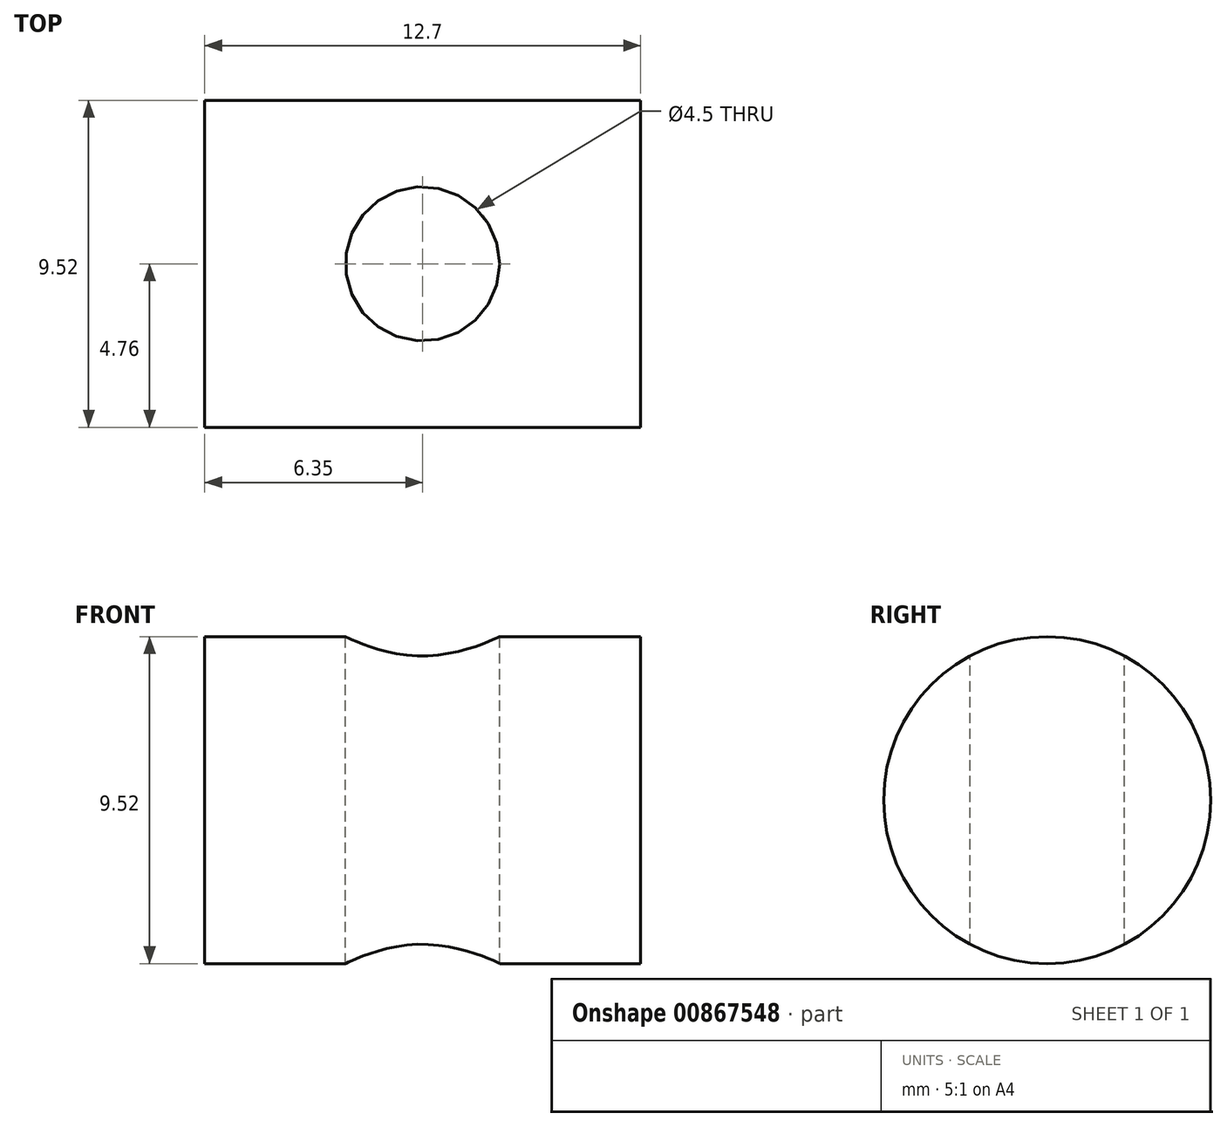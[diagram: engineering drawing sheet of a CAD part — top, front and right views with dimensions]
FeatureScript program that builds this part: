
annotation { "Feature Type Name" : "Feature", "Feature Type Description" : "" }
export const myFeature = defineFeature(function(context is Context, id is Id, definition is map)
    precondition{}
    {
        {
            var Q0;
            Q0=qCreatedBy(makeId("Right.planeOp"),FACE);
            var sketch = newSketch(context, id + "F0", { "sketchPlane" : qUnion([Q0])});
            skCircle(sketch, "E0", {"center": v(0, 33.64) * mm, "radius": 4.76 * mm});
            skPoint(sketch, "E1", {"position": v(0, 38.4) * mm});
            skSolve(sketch);
        }
        {
            var Q0;
            Q0=makeQuery(id+"F0.imprint","IMPRINT",FACE,{"disambiguationData":[TD([[makeQuery(id+"F0.imprint","IMPRINT",EDGE,{"derivedFrom":sQuery(id+"F0.wireOp",EDGE,"E0")}),1.0]])]});
            extrude(context, id + "F1", {"entities" : qUnion([Q0]), "endBound" : BoundingType.SYMMETRIC, "depth" : 12.7 * mm, "offsetDistance" : 25.4 * mm});
        }
        {
            var Q0;
            Q0=sQuery(id+"F0.wireOp",VERTEX,"E1");
            var Q1;
            Q1=qCreatedBy(makeId("Top.planeOp"),FACE);
            cPlane(context, id + "F2", {"entities" : qUnion([Q0, Q1]), "cplaneType" : CPlaneType.PLANE_POINT, "offset" : 25.4 * mm, "width" : 152.4 * mm, "height" : 152.4 * mm});
        }
        {
            var Q0;
            Q0=qCreatedBy(id+"F2.planeOp",FACE);
            var sketch = newSketch(context, id + "F3", { "sketchPlane" : qUnion([Q0])});
            skPoint(sketch, "E2.0", {"position": v(0, 0) * mm});
            skSolve(sketch);
        }
        {
            var Q0;
            Q0=sQuery(id+"F3.wireOp",VERTEX,"E2.0");
            var Q1;
            Q1=makeQuery(id+"F1.opExtrude","SWEPT_BODY",BODY,{"disambiguationData":[OSD([sQuery(id+"F0.wireOp",EDGE,"E0")])]});
            hole(context, id + "F4", {"style" : HoleStyle.SIMPLE, "endStyle" : HoleEndStyle.THROUGH, "standardTappedOrClearance" : lookupTablePath({ "standard" : "ANSI", "engagement" : "75%", "pitch" : "24 tpi", "size" : "#12", "type" : "Tapped" }), "standardBlindInLast" : lookupTablePath({ "standard" : "ANSI", "fit" : "Normal", "engagement" : "75%", "pitch" : "24 tpi", "size" : "#12", "type" : "Clearance & tapped" }), "holeDiameter" : 4.5 * mm, "majorDiameter" : 5.5 * mm, "showTappedDepth" : true, "isTappedThrough" : true, "tappedDepth" : 12.7 * mm, "tapClearance" : 3, "locations" : qUnion([Q0]), "scope" : qUnion([Q1])});
        }
    });
